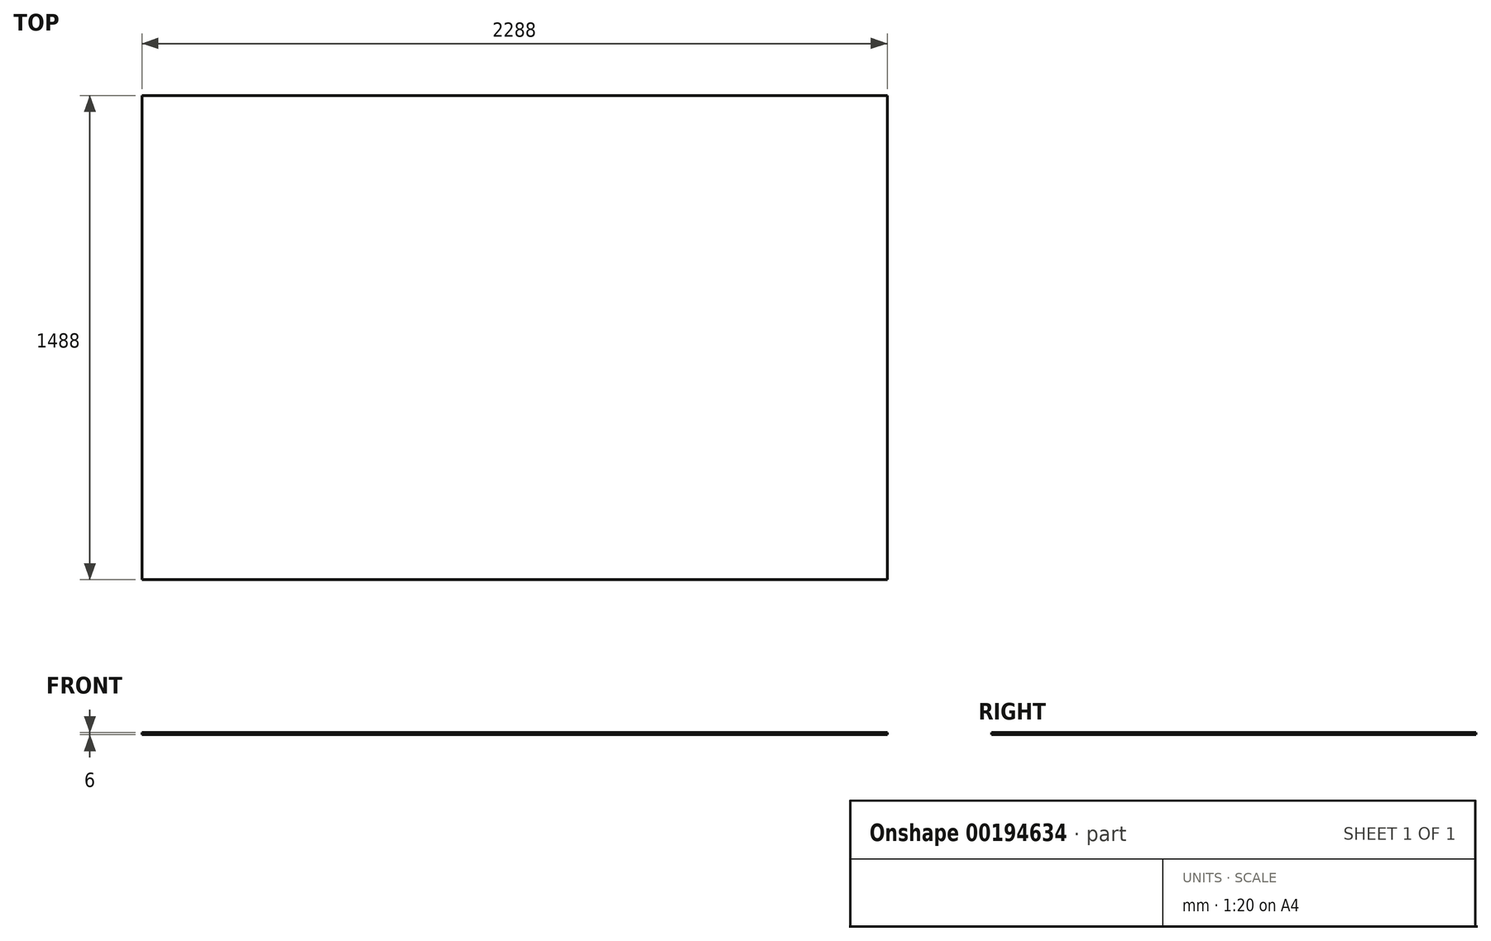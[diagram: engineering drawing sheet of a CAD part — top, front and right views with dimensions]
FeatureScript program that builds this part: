
annotation { "Feature Type Name" : "Feature", "Feature Type Description" : "" }
export const myFeature = defineFeature(function(context is Context, id is Id, definition is map)
    precondition{}
    {
        {
            var Q0;
            Q0=qCreatedBy(makeId("Top.planeOp"),FACE);
            var sketch = newSketch(context, id + "F0", { "sketchPlane" : qUnion([Q0])});
            skLineSegment(sketch, "E0.bottom", {"start": v(1144, -744) * mm, "end": v(-1144, -744) * mm});
            skLineSegment(sketch, "E0.top", {"start": v(1144, 744) * mm, "end": v(-1144, 744) * mm});
            skLineSegment(sketch, "E0.left", {"start": v(1144, -744) * mm, "end": v(1144, 744) * mm});
            skLineSegment(sketch, "E0.right", {"start": v(-1144, -744) * mm, "end": v(-1144, 744) * mm});
            skPoint(sketch, "E0.middle", {"position": v(0, 0) * mm});
            skSolve(sketch);
        }
        {
            var Q0;
            Q0 = qSketchRegion(id + "F0", true);
            extrude(context, id + "F1", {"entities" : qUnion([Q0]), "depth" : 6 * mm});
        }
    });
